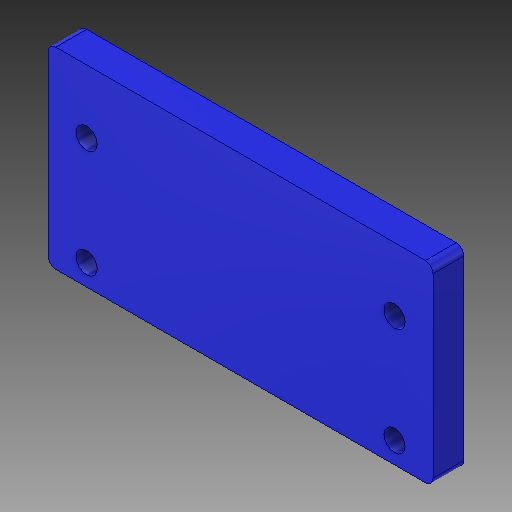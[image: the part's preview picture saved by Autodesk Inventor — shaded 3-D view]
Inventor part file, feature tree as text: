
AUTODESK INVENTOR PART (.ipt)
format: ipt  version: 2018 (Build 220112000, 112)  size: 116,224 bytes
history: native  units: mm
features: sketch x2, extrude x1, fillet x1, hole x1
ambient origin geometry x8: Origin, YZ Plane, XZ Plane, XY Plane, X Axis, Y Axis, Z Axis, Center Point
bodies: Solido1 (feature_tree)
feature tree (5):
  extrude  "Estrusione1"  Depth=100.0mm
  fillet  "Raccordo1"  Radius=50.0mm
  hole  "Foro1"  [1 undecoded]
  sketch  "Schizzo1"
  sketch  "Schizzo2"
note: 1 required parameter value undecoded (feature->parameter linkage not recoverable at this tier; creation-order binding heuristic only, values carry confidence <= 0.55)
